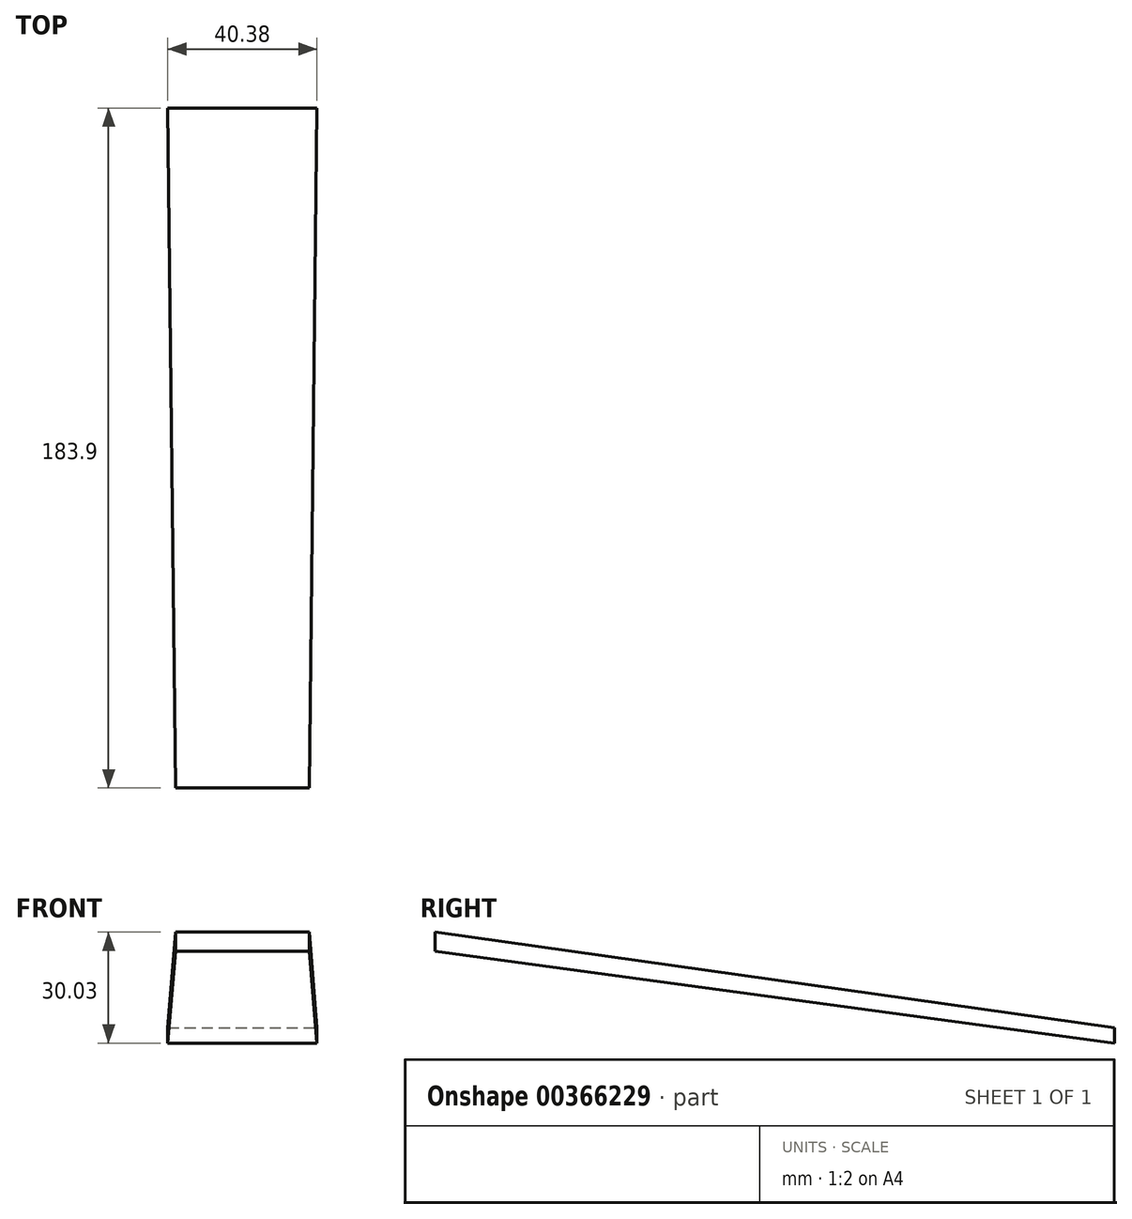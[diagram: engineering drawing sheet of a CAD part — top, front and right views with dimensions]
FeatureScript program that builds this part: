
annotation { "Feature Type Name" : "Feature", "Feature Type Description" : "" }
export const myFeature = defineFeature(function(context is Context, id is Id, definition is map)
    precondition{}
    {
        {
            var Q0;
            Q0=qCreatedBy(makeId("Front.planeOp"),FACE);
            cPlane(context, id + "F0", {"entities" : qUnion([Q0]), "cplaneType" : CPlaneType.OFFSET, "offset" : 183.9 * mm, "width" : 152.4 * mm, "height" : 152.4 * mm});
        }
        {
            var Q0;
            Q0=qCreatedBy(id+"F0.planeOp",FACE);
            var sketch = newSketch(context, id + "F1", { "sketchPlane" : qUnion([Q0])});
            skLineSegment(sketch, "E0.bottom", {"start": v(-18.12, 47.1) * mm, "end": v(18.12, 47.1) * mm});
            skLineSegment(sketch, "E0.top", {"start": v(-18.12, 41.93) * mm, "end": v(18.12, 41.93) * mm});
            skLineSegment(sketch, "E0.left", {"start": v(-18.12, 47.1) * mm, "end": v(-18.12, 41.93) * mm});
            skLineSegment(sketch, "E0.right", {"start": v(18.12, 47.1) * mm, "end": v(18.12, 41.93) * mm});
            skPoint(sketch, "E0.middle", {"position": v(0, 44.52) * mm});
            skSolve(sketch);
        }
        {
            var Q0;
            Q0=qCreatedBy(makeId("Front.planeOp"),FACE);
            var sketch = newSketch(context, id + "F2", { "sketchPlane" : qUnion([Q0])});
            skLineSegment(sketch, "E1.bottom", {"start": v(-20.19, 17.08) * mm, "end": v(20.19, 17.08) * mm});
            skLineSegment(sketch, "E1.top", {"start": v(-20.19, 21.22) * mm, "end": v(20.19, 21.22) * mm});
            skLineSegment(sketch, "E1.left", {"start": v(-20.19, 17.08) * mm, "end": v(-20.19, 21.22) * mm});
            skLineSegment(sketch, "E1.right", {"start": v(20.19, 17.08) * mm, "end": v(20.19, 21.22) * mm});
            skPoint(sketch, "E1.middle", {"position": v(0, 19.15) * mm});
            skSolve(sketch);
        }
        {
            var Q0;
            Q0=makeQuery(id+"F2.imprint","IMPRINT",FACE,{"disambiguationData":[TD([[makeQuery(id+"F2.imprint","IMPRINT",EDGE,{"derivedFrom":sQuery(id+"F2.wireOp",EDGE,"E1.bottom")}),1.0]])]});
            var Q1;
            Q1=makeQuery(id+"F1.imprint","IMPRINT",FACE,{"disambiguationData":[TD([[makeQuery(id+"F1.imprint","IMPRINT",EDGE,{"derivedFrom":sQuery(id+"F1.wireOp",EDGE,"E0.bottom")}),-1.0]])]});
            loft(context, id + "F3", {"sheetProfilesArray" : [{ "sheetProfileEntities" : qUnion([Q0]) }, { "sheetProfileEntities" : qUnion([Q1]) }]});
        }
    });
